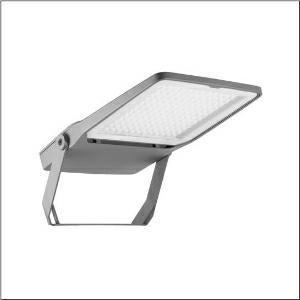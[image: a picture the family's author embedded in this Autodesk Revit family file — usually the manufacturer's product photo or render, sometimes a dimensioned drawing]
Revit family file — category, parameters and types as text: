
# Revit family: floodlight_fl_20_midi___rs17_5xa7682d1b1ac_4d76
name_source: partatom
category: Lighting Fixtures
units: mm (PartAtom-declared; Revit-internal decimal feet)

## family parameters
Cut with Voids When Loaded = No
Host = Face
Light Source = No
Part Type = Normal
Room Calculation Point = No
Round Connector Dimension = Use Diameter
Shared = No

## types (1)
- --- (1 x LED 3000K / CRI = 80 (unbekannt), 15350 lm, 3000K)
    Apparent Load = 142 VA
    CIE Flux Codes = 79 92 99 100 100
    Color Rendering = 80
    Color Temperature = 3000K
    Default Elevation = 1800 mm
    Description = Floodlight FL 20 midi, floodlight, primary light control with lens, of plastic, primary optical cover: protective disc, of toughened safety glass, transparent, light distribution: RS17, light emission: direct distribution, primary light characteristic: rotationally symmetric, installation type: surface-mounted, LED High Power LED, rated luminous flux: 15.350 lm, light colour: 830, colour temperature: 3000K, control gear: ECG Plus, control: flexible luminous flux parameterisation, time-dependent luminous flux control, digital communication interface, power reduction, overheat protection, electronic power reduction, with terminal, 5-pole, max. 2.5mm², mains connection: 220..240V, AC, 50/60Hz, rated input power: 142W, LED unit, of diecast aluminium, powder-coated, Siteco® metallic grey (DB 702S), length: 654 mm, width: 450 mm, height: 76mm, housing frame, of diecast aluminium, powder-coated, Siteco® metallic grey (DB 702S), mounting bracket, of steel, powder-coated, Siteco® metallic grey (DB 702S), DALIprotection rating (complete): IP66, insulation class (complete): insulation class II (safety insulation), certification: CE, ENEC, VDE, protection symbol: D, permissible ambient temperature for indoor applications: -40..+40°C, permissible ambient temperature for outdoor applications: -40..+50°C, standard: DIN EN 12944, packaging unit: 1 piece

Light Distribution: RS17
    Height = 76 mm
    Lamp = 1 x LED 3000K / CRI >= 80 (unbekannt)
    Lamp Light Flux = 15350 lm
    Lamp count = 1
    Length = 672 mm
    Luminous efficacy = 108 lm/W
    Manufacturer = Siteco
    ModVariant = No
    Model = 5XA7682D1B1AC
    Number of Poles = 1
    OnlyDefault = Yes
    Power Factor = 1
    Product Name = Floodlight FL 20 midi | RS17
    Product group = floodlight | pylon top
    ProductGroupID = 6101
    Protection Class = Protection class II
    Protection Degree = IP 66
    RLX_Detail_Level = 1
    RlxData = <blob elided: 92201 chars, md5=67eb6d70>
    Socket = socket
    Standby Power = 0 W
    System Light Flux = 15350 lm
    System Power = 142 W
    Type Comments = factory setting: luminous flux: 100 % | dim-lin: 254 | 489 mA
    Type Image = l_1005943.jpg
    URL = http://relux.com
    VarID = @adj_142101
    Voltage = 0 V
    Weight = 0.00 kg
    Width = 450 mm

## geometry (parser evidence)
native form markers: Blend x4, Sweep x12
no freeform markers — native parametric forms only
